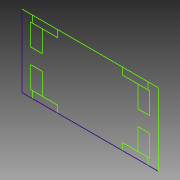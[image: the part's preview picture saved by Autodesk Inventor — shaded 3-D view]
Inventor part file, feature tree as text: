
AUTODESK INVENTOR PART (.ipt)
format: ipt  version: 2013 (Build 170138000, 138)  size: 68,608 bytes
history: native  units: in
note: dims shown in document units (in); Inventor stores cm internally (conversion verified against a paired STEP export)
features: sketch x1
ambient origin geometry x8: Origin, YZ Plane, XZ Plane, XY Plane, X Axis, Y Axis, Z Axis, Center Point
feature tree (1):
  sketch  "Sketch1"
